# Revit family: Waste_Receptacle-Bobrick-TrimLineSeries-B-35643
name_source: partatom
category: Specialty Equipment
units: mm (PartAtom-declared; Revit-internal decimal feet)

## family parameters
Cut with Voids When Loaded = No
Host = Face
OmniClass Number = 23.40.20.31
OmniClass Title = Refuse Disposal Furniture
Part Type = Normal
Room Calculation Point = No
Round Connector Dimension = Use Diameter
Shared = Yes

## types (1)
- B-35643
    ADA Compliant = Yes
    Assembly Code = E1090900
    Default Elevation = 48"
    Description = TrimLineSeries™ Recessed Waste Receptacle
    Finish = Stainless Steel-Bobrick-Type 304-Satin
    Height = 40 1/16"
    Installation Type = Recessed
    Length = 8 3/8"
    Manufacturer = Bobrick Washroom Equipment, Inc.
    Materials = Stainless Steel-Bobrick-Type 304-Satin
    Model = B-35643
    Price = Prices may vary. Please consult Manufacturer Representative for most up-to-date price list.
    Product Documentation Link = https://www.bobrick.com
    Product Page URL = https://www.bobrick.com
    Revised Date = 11/03/2020
    Specification = Recessed waste receptacle shall be Type-304 stainless steel with all-welded construction; exposed surfaces shall have satin fi nish. Door shall be Type-304, 18 gauge (1.2mm) secured to cabinet with a concealed, full-length stainless steel piano-hinge, cable door-swing limiter and equipped with two tumbler locks keyed like other Bobrick washroom accessories. Waste receptacle shall be furnished with a removable, leak-proof, rigid molded plastic waste-container with a minimum capacity of 12-gal. (45.4-L).
    URL = http://bobrick.com
    Warranty Documentation Link = https://www.bobrick.com
    Warranty Information = 1 Year Limited Warranty
    Width = 17 5/16"

## geometry (parser evidence)
native form markers: Sweep x3
no freeform markers — native parametric forms only
